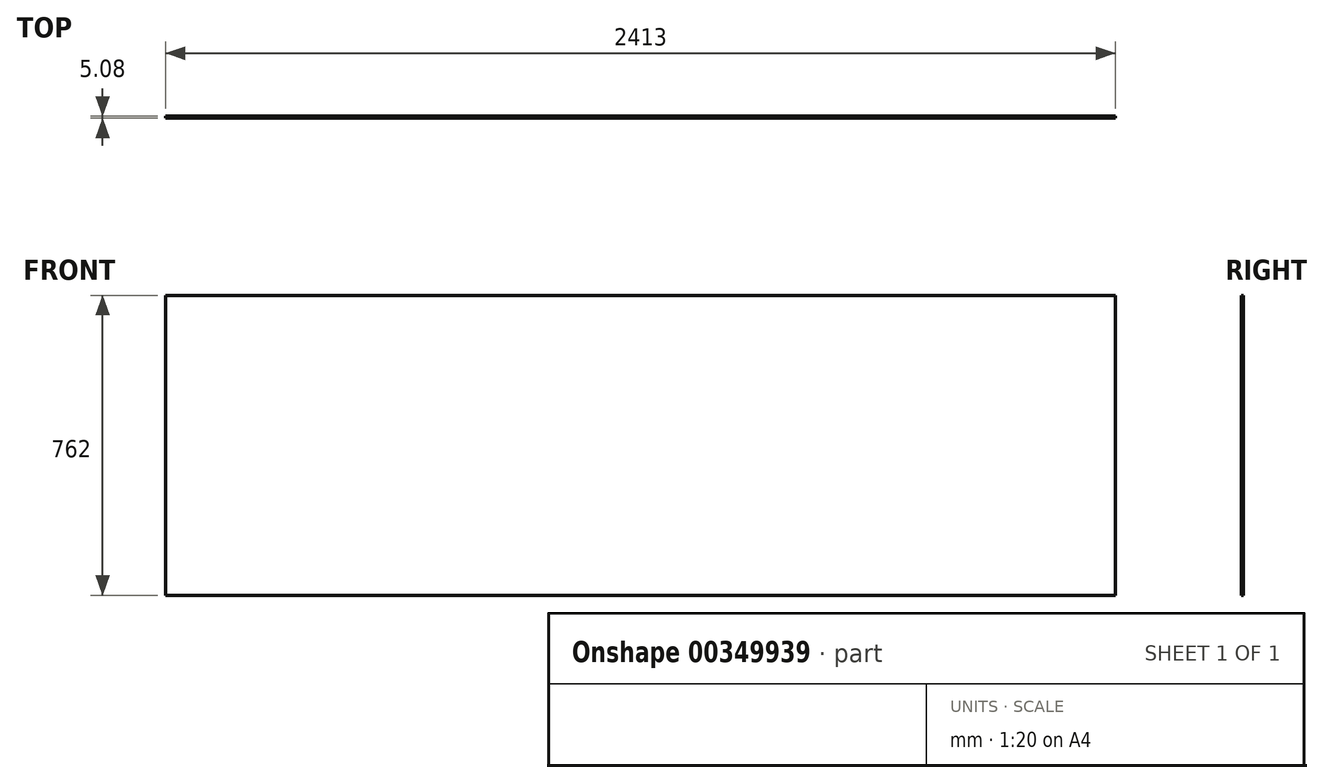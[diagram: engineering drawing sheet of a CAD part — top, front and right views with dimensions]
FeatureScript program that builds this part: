
annotation { "Feature Type Name" : "Feature", "Feature Type Description" : "" }
export const myFeature = defineFeature(function(context is Context, id is Id, definition is map)
    precondition{}
    {
        {
            var Q0;
            Q0=qCreatedBy(makeId("Front.planeOp"),FACE);
            var sketch = newSketch(context, id + "F0", { "sketchPlane" : qUnion([Q0])});
            skLineSegment(sketch, "E0.bottom", {"start": v(-57, 720.64) * mm, "end": v(2356, 720.64) * mm});
            skLineSegment(sketch, "E0.top", {"start": v(-57, -41.36) * mm, "end": v(2356, -41.36) * mm});
            skLineSegment(sketch, "E0.left", {"start": v(-57, 720.64) * mm, "end": v(-57, -41.36) * mm});
            skLineSegment(sketch, "E0.right", {"start": v(2356, 720.64) * mm, "end": v(2356, -41.36) * mm});
            skSolve(sketch);
        }
        {
            var Q0;
            Q0 = qSketchRegion(id + "F0", true);
            extrude(context, id + "F1", {"entities" : qUnion([Q0]), "depth" : 5.08 * mm, "offsetDistance" : 25.4 * mm});
        }
    });
